# Revit family: DSI-FW119_Smoke-and-Fire-Curtain_Over-Under-Headbox_Door-Systems
name_source: partatom
category: Doors
units: mm (PartAtom-declared; Revit-internal decimal feet)

## family parameters
Always vertical = Yes
Cut with Voids When Loaded = No
Host = Wall
OmniClass Number = 23.30.10.00
OmniClass Title = Doors
Room Calculation Point = No
Shared = No

## types (3) — shared parameters
Analytic Construction = <None>
CAD Details = https://www.arcat.com
Curtain Finish = HS690-SS FABRIC- FW119
CurtainDrop_Viz = Yes
Define Thermal Properties by = Schematic Type
Frame Finish = Metal - Steel - Primed
Frame Projection Ext. = 0' - 1"
Frame Projection Int. = 0' - 1"
Frame Width = 0' - 3"
Function = Interior
Height = 9' - 0"
Keynote = 08 33 44
Manufacturer = Door Systems
Model = DSI-FW119
Product Page URL = https://www.arcat.com
Specification = https://www.arcat.com
URL = https://www.doorsysinc.com
Wall Closure = By host
Width = 7' - 0"

## per-type parameters (varying)
| type | Head Box Height | Head Box Width |
| 9" x 15" Head-box #1 | 1' - 3" | 0' - 9" |
| 10" x 18" Head-box #2 | 1' - 6" | 0' - 10" |
| 12" x 21" Head-box #3 | 1' - 9" | 1' - 0" |

## geometry (parser evidence)
native form markers: Sweep x5
no freeform markers — native parametric forms only
